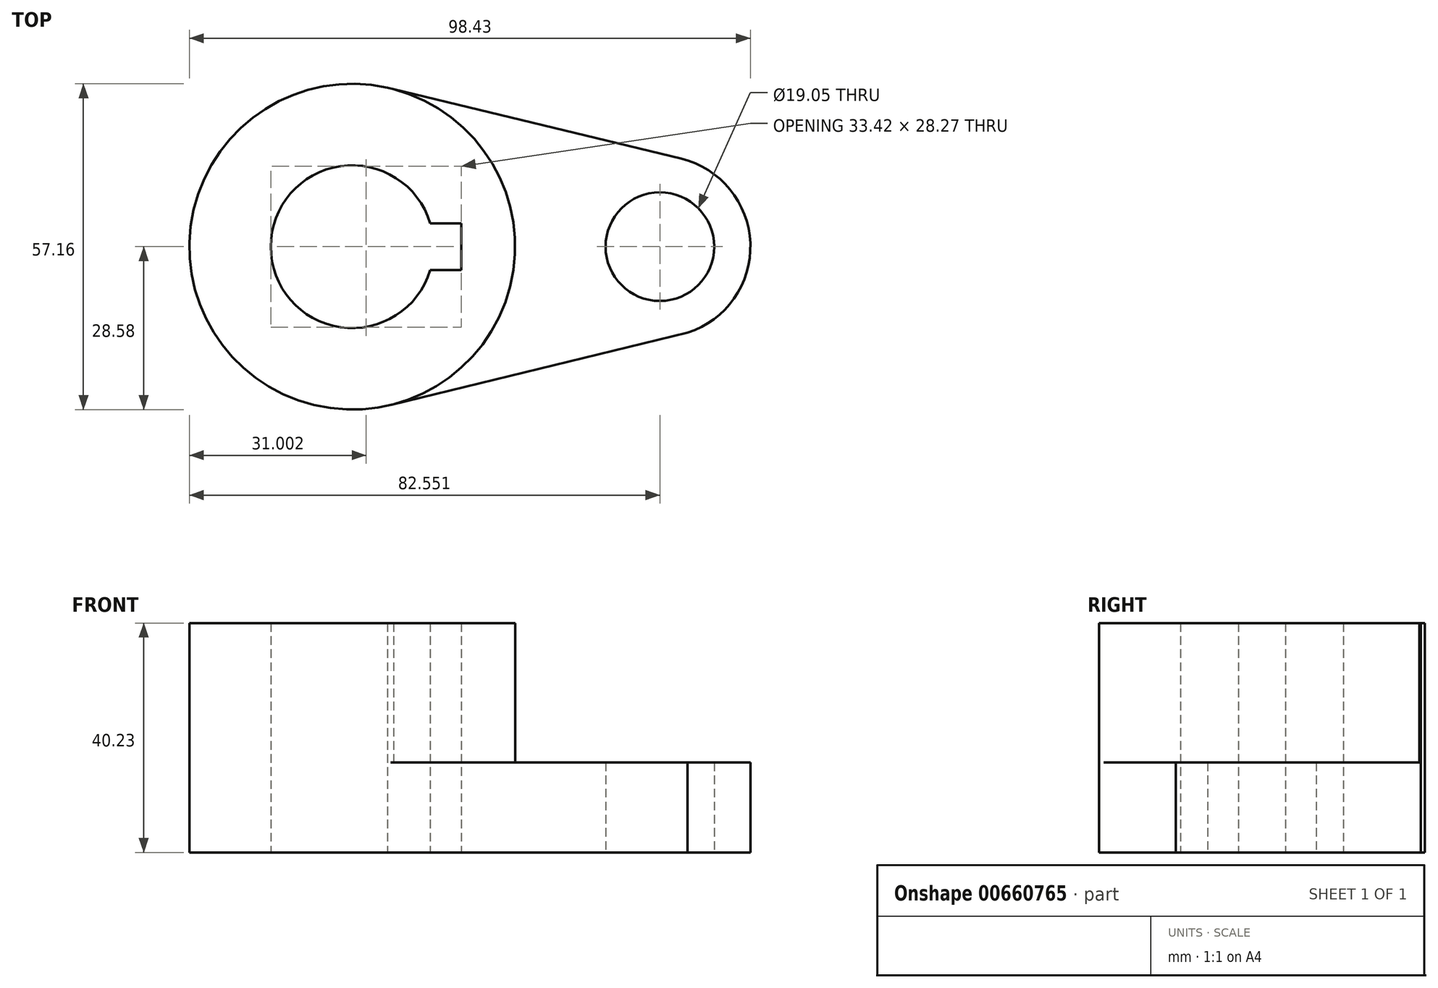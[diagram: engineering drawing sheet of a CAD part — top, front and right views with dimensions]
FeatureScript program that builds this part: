
annotation { "Feature Type Name" : "Feature", "Feature Type Description" : "" }
export const myFeature = defineFeature(function(context is Context, id is Id, definition is map)
    precondition{}
    {
        {
            var Q0;
            Q0=qCreatedBy(makeId("Top.planeOp"),FACE);
            var sketch = newSketch(context, id + "F0", { "sketchPlane" : qUnion([Q0])});
            skCircle(sketch, "E0", {"center": v(-32.52, 0) * mm, "radius": 28.58 * mm});
            skArc(sketch, "E1", {"start": v(-18.84, 4.12) * mm, "mid": v(-46.81, 0) * mm, "end": v(-18.84, -4.12) * mm});
            skCircle(sketch, "E2", {"center": v(-32.52, 0) * mm, "radius": 25.4 * mm});
            skLineSegment(sketch, "E3", {"start": v(-18.84, 4.12) * mm, "end": v(-13.39, 4.12) * mm});
            skLineSegment(sketch, "E4", {"start": v(-13.39, 4.12) * mm, "end": v(-13.39, -4.12) * mm});
            skLineSegment(sketch, "E5", {"start": v(-13.39, -4.12) * mm, "end": v(-18.84, -4.12) * mm});
            skCircle(sketch, "E6", {"center": v(21.45, 0) * mm, "radius": 9.53 * mm});
            skArc(sketch, "E7", {"start": v(24.06, -15.66) * mm, "mid": v(37.32, -0.57) * mm, "end": v(25.18, 15.43) * mm});
            skLineSegment(sketch, "E8", {"start": v(-26.32, 27.9) * mm, "end": v(25.18, 15.43) * mm});
            skLineSegment(sketch, "E9", {"start": v(26.32, -15.11) * mm, "end": v(-25.78, -27.77) * mm});
            skSolve(sketch);
        }
        {
            var Q0;
            Q0=makeQuery(id+"F0.imprint","IMPRINT",FACE,{"disambiguationData":[TD([[makeQuery(id+"F0.imprint","IMPRINT",EDGE,{"derivedFrom":sQuery(id+"F0.wireOp",EDGE,"E2")}),-1.0]])]});
            var Q1;
            Q1=makeQuery(id+"F0.imprint","IMPRINT",FACE,{"disambiguationData":[TD([[makeQuery(id+"F0.imprint","IMPRINT",EDGE,{"derivedFrom":sQuery(id+"F0.wireOp",EDGE,"E1")}),-1.0]])]});
            extrude(context, id + "F1", {"entities" : qUnion([Q0, Q1]), "depth" : 40.23 * mm, "offsetDistance" : 25.4 * mm});
        }
        {
            var Q0;
            Q0=makeQuery(id+"F0.imprint","IMPRINT",FACE,{"disambiguationData":[TD([[makeQuery(id+"F0.imprint","IMPRINT",EDGE,{"derivedFrom":sQuery(id+"F0.wireOp",EDGE,"E6")}),-1.0]])]});
            extrude(context, id + "F2", {"entities" : qUnion([Q0]), "operationType" : NewBodyOperationType.ADD, "depth" : 15.77 * mm, "offsetDistance" : 25.4 * mm});
        }
    });
